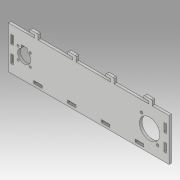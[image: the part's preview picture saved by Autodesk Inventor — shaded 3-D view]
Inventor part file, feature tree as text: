
AUTODESK INVENTOR PART (.ipt)
format: ipt  version: 2019.3 (Build 233278000, 278)  size: 223,232 bytes
history: native  units: mm
features: extrude x1, sketch x1
ambient origin geometry x8: Origin, YZ Plane, XZ Plane, XY Plane, X Axis, Y Axis, Z Axis, Center Point
bodies: Body1 (feature_tree)
feature tree (2):
  extrude  "Extrusion3"  Depth=50.0mm
  sketch  "Sketch1"  dims[d6=190.0mm d7=50.0mm d19=20.0mm d23=10.0mm d24=3.0mm d25=3.0mm d26=4.0mm d27=1.0mm d28=45.0mm d29=45.0mm d30=45.0mm d31=31.0mm d32=10.0mm d33=3.0mm d34=3.0mm d35=10.0mm d36=10.0mm d37=3.0mm d38=24.0mm d39=5.0mm d40=15.5mm d41=10.25mm d42=7.0mm d43=2.5mm d44=14.5mm d45=14.5mm d46=7.25mm d47=7.25mm d48=5.0mm d51=10.0mm d52=30.0mm d53=30.0mm d54=30.0mm d55=30.0mm d56=3.0mm d57=3.0mm d60=3.0mm d61=31.0mm d62=26.0mm d63=2.0mm d64=2.0mm d65=2.0mm d66=2.0mm d67=3.0mm d68=0.0mm]
